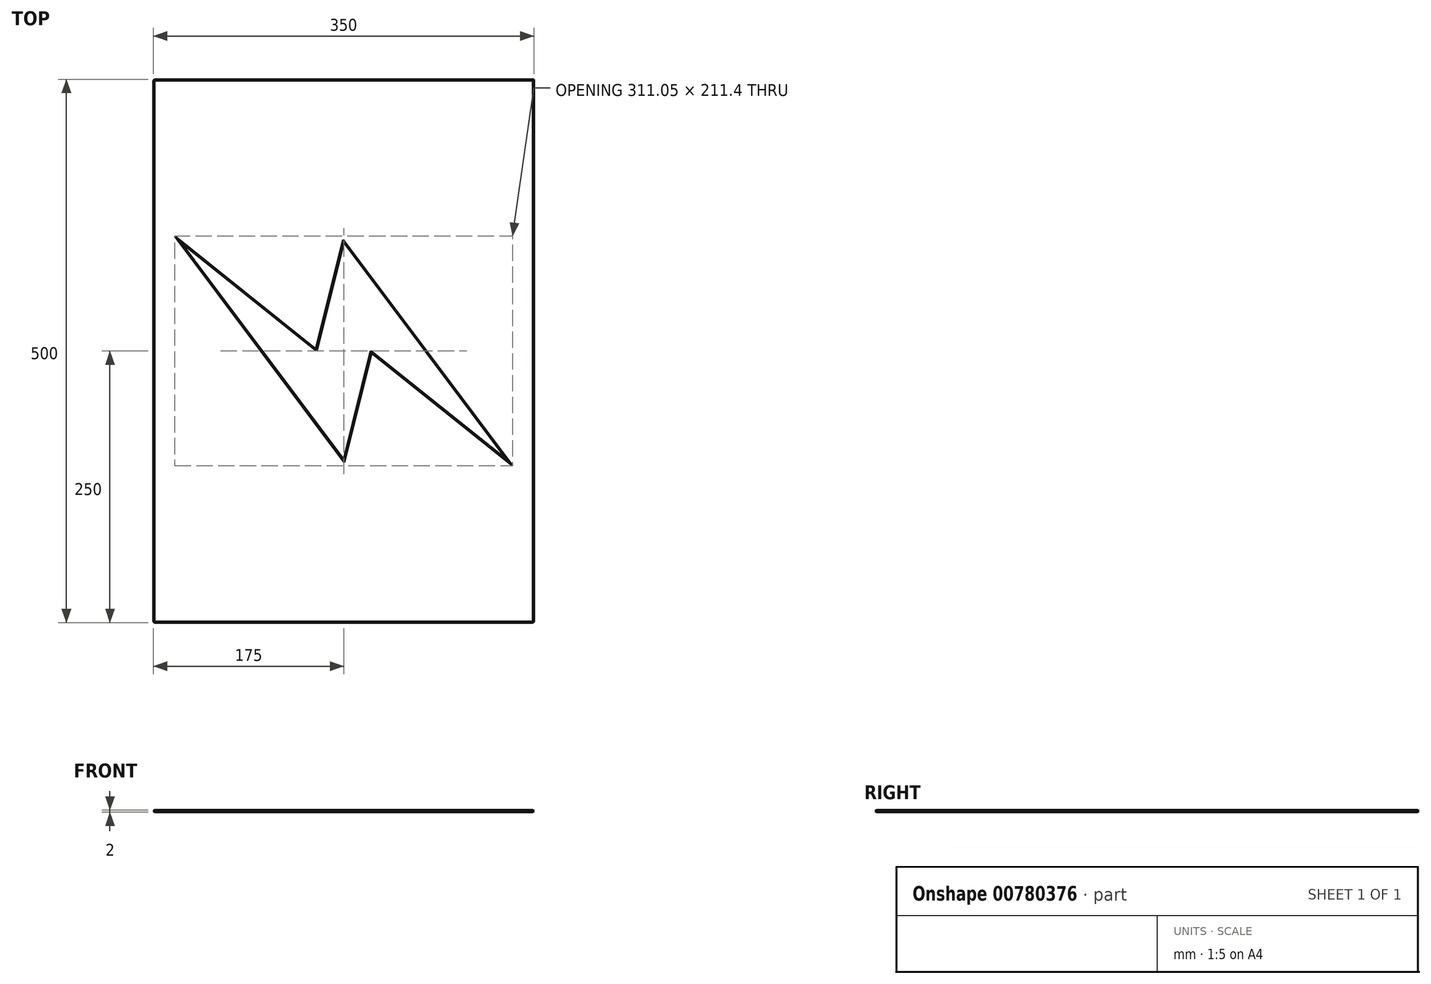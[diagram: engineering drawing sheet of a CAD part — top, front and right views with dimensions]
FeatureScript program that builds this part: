
annotation { "Feature Type Name" : "Feature", "Feature Type Description" : "" }
export const myFeature = defineFeature(function(context is Context, id is Id, definition is map)
    precondition{}
    {
        {
            var Q0;
            Q0=qCreatedBy(makeId("Top.planeOp"),FACE);
            var sketch = newSketch(context, id + "F0", { "sketchPlane" : qUnion([Q0])});
            skLineSegment(sketch, "E0.bottom", {"start": v(175, -250) * mm, "end": v(-175, -250) * mm});
            skLineSegment(sketch, "E0.top", {"start": v(175, 250) * mm, "end": v(-175, 250) * mm});
            skLineSegment(sketch, "E0.left", {"start": v(175, -250) * mm, "end": v(175, 250) * mm});
            skLineSegment(sketch, "E0.right", {"start": v(-175, -250) * mm, "end": v(-175, 250) * mm});
            skPoint(sketch, "E0.middle", {"position": v(0, 0) * mm});
            skLineSegment(sketch, "E1.bottom", {"start": v(0, 0) * mm, "end": v(0, 0) * mm});
            skLineSegment(sketch, "E1.top", {"start": v(0, 0) * mm, "end": v(0, 0) * mm});
            skLineSegment(sketch, "E1.left", {"start": v(0, 0) * mm, "end": v(0, 0) * mm});
            skLineSegment(sketch, "E1.right", {"start": v(0, 0) * mm, "end": v(0, 0) * mm});
            skLineSegment(sketch, "E2.bottom", {"start": v(150, -100) * mm, "end": v(-150, -100) * mm});
            skLineSegment(sketch, "E2.top", {"start": v(150, 100) * mm, "end": v(-150, 100) * mm});
            skLineSegment(sketch, "E2.left", {"start": v(150, -100) * mm, "end": v(150, 100) * mm});
            skLineSegment(sketch, "E2.right", {"start": v(-150, -100) * mm, "end": v(-150, 100) * mm});
            skLineSegment(sketch, "E3.bottom", {"start": v(150, -100) * mm, "end": v(150, -100) * mm});
            skLineSegment(sketch, "E3.top", {"start": v(150, -100) * mm, "end": v(150, -100) * mm});
            skLineSegment(sketch, "E3.left", {"start": v(150, -100) * mm, "end": v(150, -100) * mm});
            skLineSegment(sketch, "E3.right", {"start": v(150, -100) * mm, "end": v(150, -100) * mm});
            skLineSegment(sketch, "E4", {"start": v(-150, 100) * mm, "end": v(0, -100) * mm});
            skLineSegment(sketch, "E5", {"start": v(0, -100) * mm, "end": v(150, -100) * mm});
            skLineSegment(sketch, "E6", {"start": v(150, -100) * mm, "end": v(0, 100) * mm});
            skLineSegment(sketch, "E7", {"start": v(0, 100) * mm, "end": v(-150, 100) * mm});
            skLineSegment(sketch, "E8", {"start": v(-150, 100) * mm, "end": v(-150, 100) * mm});
            skLineSegment(sketch, "E9", {"start": v(-150, 100) * mm, "end": v(-25, 0) * mm});
            skLineSegment(sketch, "E10", {"start": v(150, -100) * mm, "end": v(25, 0) * mm});
            skPoint(sketch, "E10.endSnap0", {"position": v(75, 0) * mm});
            skLineSegment(sketch, "E11", {"start": v(0, 100) * mm, "end": v(-25, 0) * mm});
            skLineSegment(sketch, "E12", {"start": v(25, 0) * mm, "end": v(0, -100) * mm});
            skSolve(sketch);
        }
        {
            var Q0;
            {var subQ0=sQuery(id+"F0.wireOp",EDGE,"E2.right");Q0=makeQuery(id+"F0.imprint","IMPRINT",FACE,{"disambiguationData":[TD([[makeQuery(id+"F0.imprint","IMPRINT",EDGE,{"derivedFrom":subQ0}),-1.0]])]});}
            var Q1;
            {var subQ0=sQuery(id+"F0.wireOp",EDGE,"E9");Q1=makeQuery(id+"F0.imprint","IMPRINT",FACE,{"disambiguationData":[TD([[makeQuery(id+"F0.imprint","IMPRINT",EDGE,{"derivedFrom":subQ0}),1.0]])]});}
            var Q2;
            Q2=makeQuery(id+"F0.imprint","IMPRINT",FACE,{"disambiguationData":[TD([[makeQuery(id+"F0.imprint","IMPRINT",EDGE,{"derivedFrom":sQuery(id+"F0.wireOp",EDGE,"E0.bottom")}),-1.0]])]});
            var Q3;
            {var subQ0=sQuery(id+"F0.wireOp",EDGE,"E2.left");Q3=makeQuery(id+"F0.imprint","IMPRINT",FACE,{"disambiguationData":[TD([[makeQuery(id+"F0.imprint","IMPRINT",EDGE,{"derivedFrom":subQ0}),1.0]])]});}
            var Q4;
            {var subQ0=sQuery(id+"F0.wireOp",EDGE,"E10");Q4=makeQuery(id+"F0.imprint","IMPRINT",FACE,{"disambiguationData":[TD([[makeQuery(id+"F0.imprint","IMPRINT",EDGE,{"derivedFrom":subQ0}),1.0]])]});}
            extrude(context, id + "F1", {"entities" : qUnion([Q0, Q1, Q2, Q3, Q4]), "depth" : 2 * mm, "offsetDistance" : 25 * mm});
        }
        {
            var Q0;
            Q0=makeQuery(id+"F1.opExtrude","CAP_FACE",FACE,{"disambiguationData":[OSD([sQuery(id+"F0.wireOp",EDGE,"E0.bottom"),sQuery(id+"F0.wireOp",EDGE,"E0.top"),sQuery(id+"F0.wireOp",EDGE,"E0.left"),sQuery(id+"F0.wireOp",EDGE,"E0.right"),sQuery(id+"F0.wireOp",EDGE,"E4"),sQuery(id+"F0.wireOp",EDGE,"E6"),sQuery(id+"F0.wireOp",EDGE,"E9"),sQuery(id+"F0.wireOp",EDGE,"E10"),sQuery(id+"F0.wireOp",EDGE,"E11"),sQuery(id+"F0.wireOp",EDGE,"E12")])],"isStart":false});
            var Q1;
            Q1=makeQuery(id+"F1.opExtrude","CAP_FACE",FACE,{"disambiguationData":[OSD([sQuery(id+"F0.wireOp",EDGE,"E0.bottom"),sQuery(id+"F0.wireOp",EDGE,"E0.top"),sQuery(id+"F0.wireOp",EDGE,"E0.left"),sQuery(id+"F0.wireOp",EDGE,"E0.right"),sQuery(id+"F0.wireOp",EDGE,"E4"),sQuery(id+"F0.wireOp",EDGE,"E6"),sQuery(id+"F0.wireOp",EDGE,"E9"),sQuery(id+"F0.wireOp",EDGE,"E10"),sQuery(id+"F0.wireOp",EDGE,"E11"),sQuery(id+"F0.wireOp",EDGE,"E12")])],"isStart":true});
            var Q2;
            Q2=makeQuery(id+"F1.opExtrude","SWEPT_FACE",FACE,{"disambiguationData":[OSD([sQuery(id+"F0.wireOp",EDGE,"E0.bottom")])]});
            var Q3;
            Q3=makeQuery(id+"F1.opExtrude","SWEPT_EDGE",EDGE,{"disambiguationData":[OSD([sQuery(id+"F0.wireOp",EDGE,"E0.bottom"),sQuery(id+"F0.wireOp",EDGE,"E0.left")])]});
            var Q4;
            Q4=makeQuery(id+"F1.opExtrude","SWEPT_EDGE",EDGE,{"disambiguationData":[OSD([sQuery(id+"F0.wireOp",EDGE,"E0.bottom"),sQuery(id+"F0.wireOp",EDGE,"E0.right")])]});
            var Q5;
            Q5=makeQuery(id+"F1.opExtrude","SWEPT_EDGE",EDGE,{"disambiguationData":[OSD([sQuery(id+"F0.wireOp",EDGE,"E0.top"),sQuery(id+"F0.wireOp",EDGE,"E0.right")])]});
            chamfer(context, id + "F2", {"entities" : qUnion([Q0, Q1, Q2, Q3, Q4, Q5]), "width" : 1 * mm, "tangentPropagation" : true});
        }
    });
